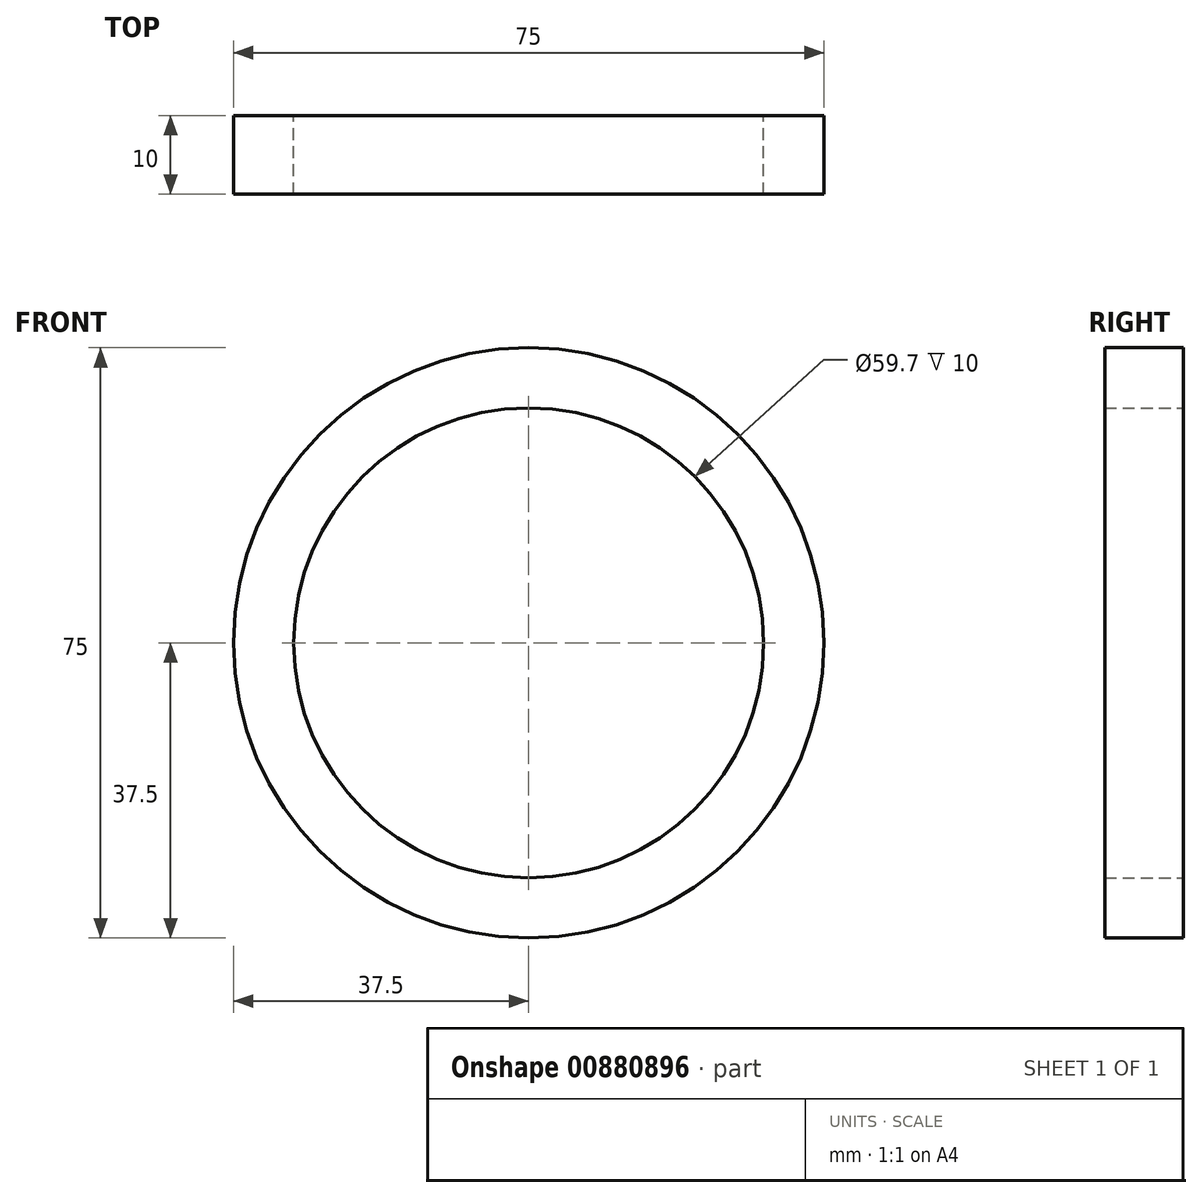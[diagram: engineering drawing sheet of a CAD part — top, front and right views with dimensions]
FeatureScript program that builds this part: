
annotation { "Feature Type Name" : "Feature", "Feature Type Description" : "" }
export const myFeature = defineFeature(function(context is Context, id is Id, definition is map)
    precondition{}
    {
        {
            var Q0;
            Q0=qCreatedBy(makeId("Front.planeOp"),FACE);
            var sketch = newSketch(context, id + "F0", { "sketchPlane" : qUnion([Q0])});
            skCircle(sketch, "E0", {"center": v(0, 0) * mm, "radius": 29.85 * mm});
            skCircle(sketch, "E1", {"center": v(0, 0) * mm, "radius": 37.5 * mm});
            skSolve(sketch);
        }
        {
            var Q0;
            Q0=makeQuery(id+"F0.imprint","IMPRINT",FACE,{"disambiguationData":[TD([[makeQuery(id+"F0.imprint","IMPRINT",EDGE,{"derivedFrom":sQuery(id+"F0.wireOp",EDGE,"E0")}),-1.0]])]});
            extrude(context, id + "F1", {"entities" : qUnion([Q0]), "depth" : 10 * mm, "offsetDistance" : 25 * mm});
        }
    });
